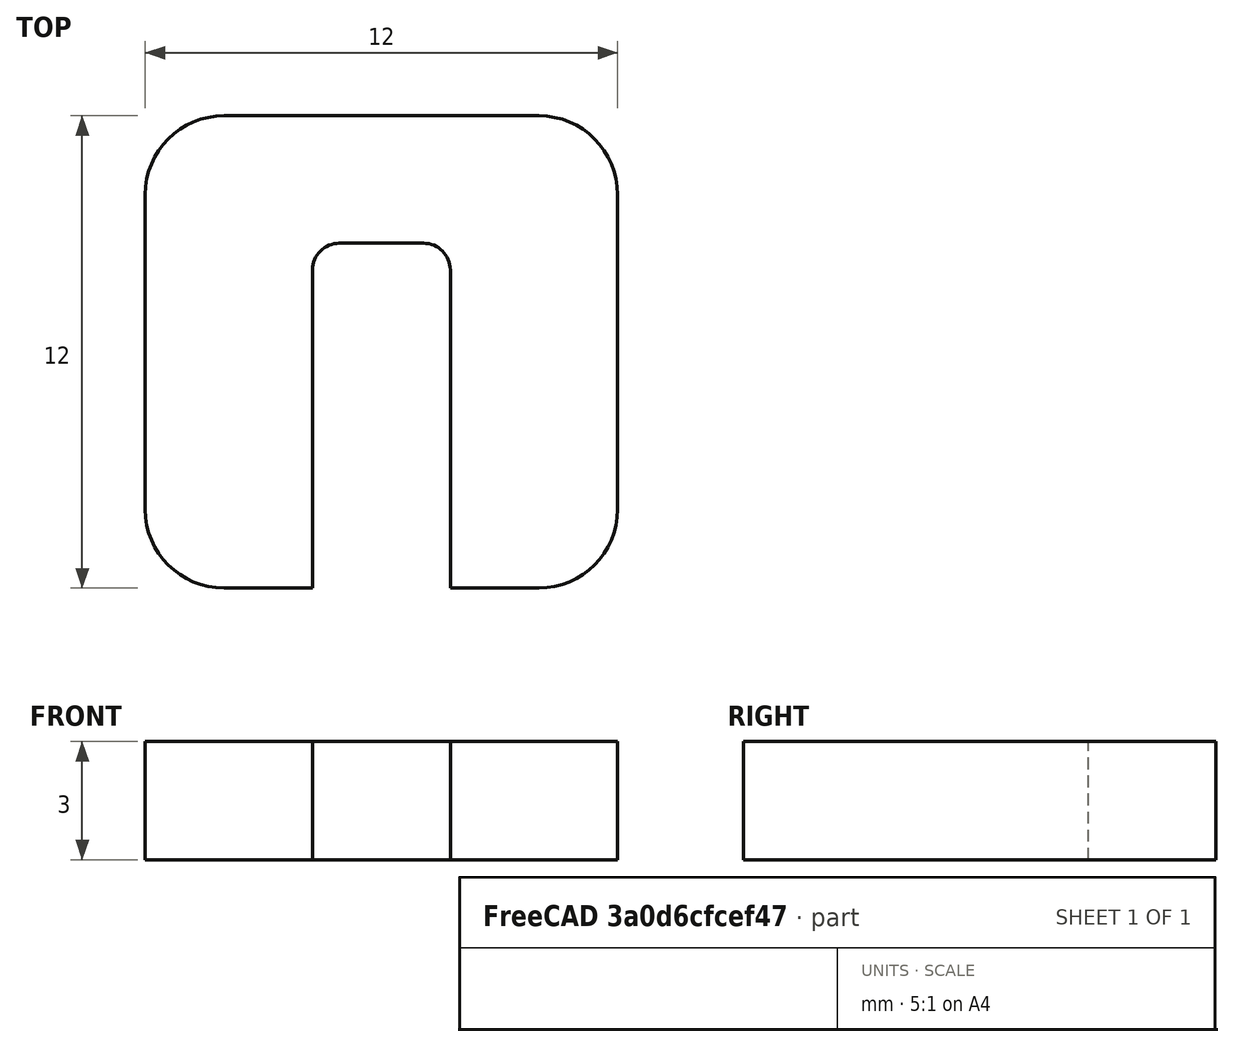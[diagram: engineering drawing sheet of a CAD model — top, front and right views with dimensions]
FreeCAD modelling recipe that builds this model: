
FCSTD DOCUMENT  (FreeCAD 1.1R44348 (Git))
Label: rpi_dev_box_cable_washer
License: All rights reserved
LicenseURL: https://en.wikipedia.org/wiki/All_rights_reserved
objects: App::Point×1, Sketcher::SketchObject×1, PartDesign::Pad×1, PartDesign::Body×1
note: 6 computed .brp shape members not serialized (recipe doc carries the construction recipe); baked Part::Feature solids carry a one-line shape summary decoded from their .brp

FEATURE [App::Point] Origin001
  Role = Origin
FEATURE [Sketcher::SketchObject] Sketch
  ArcFitTolerance = 1e-06
  AttachmentSupport = -> [Origin]
  ExternalTypes = [0]
  FullyConstrained = false
  MakeInternals = false
  MapMode = 5
  sketch-geometry (20):
    g0: LineSegment StartX=-6 StartY=4 StartZ=0 EndX=-6 EndY=-4 EndZ=0
    g1: LineSegment StartX=-4 StartY=-6 StartZ=0 EndX=-1.75 EndY=-6 EndZ=0
    g2: LineSegment StartX=6 StartY=-4 StartZ=0 EndX=6 EndY=4 EndZ=0
    g3: LineSegment StartX=4 StartY=6 StartZ=0 EndX=-4 EndY=6 EndZ=0
    g4: ArcOfCircle CenterX=-4 CenterY=4 CenterZ=0 NormalX=0 NormalY=0 NormalZ=1 AngleXU=0 Radius=2 StartAngle=1.5708 EndAngle=3.14159
    g5: GeomPoint [constr] X=-6 Y=6 Z=0
    g6: ArcOfCircle CenterX=-4 CenterY=-4 CenterZ=0 NormalX=0 NormalY=0 NormalZ=1 AngleXU=0 Radius=2 StartAngle=3.14159 EndAngle=4.71239
    g7: GeomPoint [constr] X=-6 Y=-6 Z=0
    g8: ArcOfCircle CenterX=4 CenterY=-4 CenterZ=0 NormalX=0 NormalY=0 NormalZ=1 AngleXU=0 Radius=2 StartAngle=4.71239 EndAngle=6.28319
    g9: GeomPoint [constr] X=6 Y=-6 Z=0
    g10: ArcOfCircle CenterX=4 CenterY=4 CenterZ=0 NormalX=0 NormalY=0 NormalZ=1 AngleXU=0 Radius=2 StartAngle=0 EndAngle=1.5708
    g11: GeomPoint [constr] X=6 Y=6 Z=0
    g12: LineSegment StartX=1.75 StartY=-6 StartZ=0 EndX=1.75 EndY=2.08327 EndZ=0
    g13: LineSegment StartX=1.07031 StartY=2.76296 StartZ=0 EndX=-1.07031 EndY=2.76296 EndZ=0
    g14: LineSegment StartX=-1.75 StartY=2.08327 StartZ=0 EndX=-1.75 EndY=-6 EndZ=0
    g15: LineSegment StartX=1.75 StartY=-6 StartZ=0 EndX=4 EndY=-6 EndZ=0
    g16: ArcOfCircle CenterX=-1.07031 CenterY=2.08327 CenterZ=0 NormalX=0 NormalY=0 NormalZ=1 AngleXU=0 Radius=0.679688 StartAngle=1.5708 EndAngle=3.14159
    g17: GeomPoint [constr] X=-1.75 Y=2.76296 Z=0
    g18: ArcOfCircle CenterX=1.07031 CenterY=2.08327 CenterZ=0 NormalX=0 NormalY=0 NormalZ=1 AngleXU=0 Radius=0.679688 StartAngle=0 EndAngle=1.5708
    g19: GeomPoint [constr] X=1.75 Y=2.76296 Z=0
  constraints (43):
    c: Vertical(g0)
    c: Vertical(g2)
    c: Horizontal(g3)
    c: DistanceX(g7,g9) = 12
    c: DistanceY(g9,g11) = 12
    c: Symmetric(g5,g9,g-1)
    c: PointOnObject(g5,g3)
    c: PointOnObject(g5,g0)
    c: Tangent(g3,g4) = -1.5708
    c: Tangent(g0,g4) = -1.5708
    c: PointOnObject(g7,g0)
    c: Tangent(g0,g6) = -1.5708
    c: Tangent(g1,g6) = -1.5708
    c: PointOnObject(g9,g2)
    c: Tangent(g15,g8) = -1.5708
    c: Tangent(g2,g8) = -1.5708
    c: PointOnObject(g11,g3)
    c: PointOnObject(g11,g2)
    c: Tangent(g3,g10) = -1.5708
    c: Tangent(g2,g10) = -1.5708
    c: Equal(g4,g10)
    c: Equal(g10,g8)
    c: Equal(g8,g6)
    c: Radius(g4) = 2
    c: Vertical(g12)
    c: Vertical(g14)
    c: Distance(g19,g17) = 3.5
    c: Symmetric(g19,g17,g-2)
    c: Horizontal(g1)
    c: Horizontal(g15)
    c: PointOnObject(g7,g1)
    c: PointOnObject(g9,g15)
    c: Coincident(g14,g1)
    c: Coincident(g15,g12)
    c: PointOnObject(g17,g14)
    c: PointOnObject(g17,g13)
    c: Tangent(g14,g16) = -1.5708
    c: Tangent(g13,g16) = -1.5708
    c: PointOnObject(g19,g13)
    c: PointOnObject(g19,g12)
    c: Tangent(g13,g18) = -1.5708
    c: Tangent(g12,g18) = -1.5708
    c: Equal(g18,g16)
FEATURE [PartDesign::Pad] Pad
  Direction = (0,0,1)
  Length = 3
  Length2 = 10
  Profile = -> Sketch
  ReferenceAxis = -> Sketch [N_Axis]
  Refine = true
  SideType = 0
  Suppressed = false
  Type = 0
  Type2 = 0
FEATURE [PartDesign::Body] Body
  AllowCompound = true
  Group = -> [Sketch,Pad]
  Origin = -> Origin
  Tip = -> Pad
